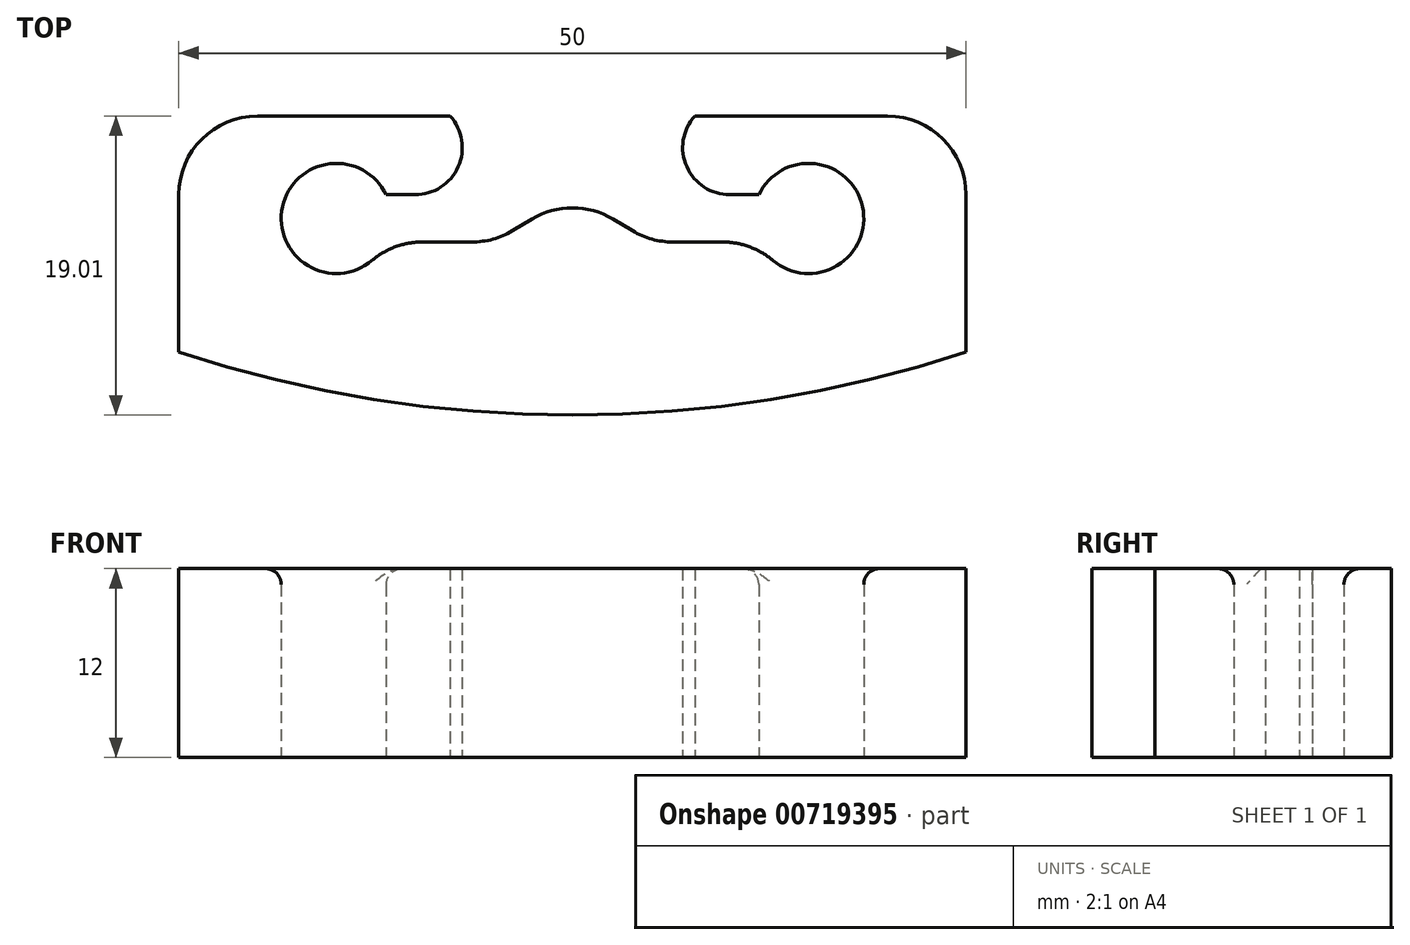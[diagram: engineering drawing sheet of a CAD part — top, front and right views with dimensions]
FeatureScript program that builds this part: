
annotation { "Feature Type Name" : "Feature", "Feature Type Description" : "" }
export const myFeature = defineFeature(function(context is Context, id is Id, definition is map)
    precondition{}
    {
        {
            var Q0;
            Q0=qCreatedBy(makeId("Top.planeOp"),FACE);
            var sketch = newSketch(context, id + "F0", { "sketchPlane" : qUnion([Q0])});
            skLineSegment(sketch, "E0", {"start": v(-25, -8.5) * mm, "end": v(-25, 1.5) * mm});
            skLineSegment(sketch, "E1", {"start": v(-20, 6.5) * mm, "end": v(-7.77, 6.5) * mm});
            skLineSegment(sketch, "E2", {"start": v(-10, 1.5) * mm, "end": v(-11.84, 1.5) * mm});
            skLineSegment(sketch, "E3", {"start": v(-9.52, -1.5) * mm, "end": v(-6.38, -1.5) * mm});
            skLineSegment(sketch, "E4", {"start": v(-3.81, -0.79) * mm, "end": v(-2.57, -0.04) * mm});
            skArc(sketch, "E5", {"start": v(-11.84, 1.5) * mm, "mid": v(-18.42, 0.74) * mm, "end": v(-12.74, -2.68) * mm});
            skArc(sketch, "E6", {"start": v(-10, 1.5) * mm, "mid": v(-7.26, 3.28) * mm, "end": v(-7.77, 6.5) * mm});
            skLineSegment(sketch, "E7.MirrorCS", {"start": v(9.52, -1.5) * mm, "end": v(6.38, -1.5) * mm});
            skLineSegment(sketch, "E8.MirrorCS", {"start": v(3.81, -0.79) * mm, "end": v(2.57, -0.04) * mm});
            skLineSegment(sketch, "E9.MirrorCS", {"start": v(20, 6.5) * mm, "end": v(7.77, 6.5) * mm});
            skLineSegment(sketch, "E10.MirrorCS", {"start": v(10, 1.5) * mm, "end": v(11.84, 1.5) * mm});
            skLineSegment(sketch, "E11.MirrorCS", {"start": v(25, -8.5) * mm, "end": v(25, 1.5) * mm});
            skArc(sketch, "E12.MirrorCS", {"start": v(11.84, 1.5) * mm, "mid": v(18.42, 0.74) * mm, "end": v(12.74, -2.68) * mm});
            skArc(sketch, "E13.MirrorCS", {"start": v(10, 1.5) * mm, "mid": v(7.26, 3.28) * mm, "end": v(7.77, 6.5) * mm});
            skArc(sketch, "E14", {"start": v(-25, -8.5) * mm, "mid": v(0, -12.5) * mm, "end": v(25, -8.5) * mm});
            skLineSegment(sketch, "E15", {"start": v(-30.94, 0) * mm, "end": v(26.36, 0) * mm, "construction": true});
            skPoint(sketch, "E16.visualSharp", {"position": v(-25, 6.5) * mm});
            skArc(sketch, "E16.filletArc", {"start": v(-20, 6.5) * mm, "mid": v(-23.54, 5.04) * mm, "end": v(-25, 1.5) * mm});
            skPoint(sketch, "E17.visualSharp", {"position": v(25, 6.5) * mm});
            skArc(sketch, "E17.filletArc", {"start": v(25, 1.5) * mm, "mid": v(23.54, 5.04) * mm, "end": v(20, 6.5) * mm});
            skPoint(sketch, "E18.visualSharp", {"position": v(-5, -1.5) * mm});
            skArc(sketch, "E18.filletArc", {"start": v(-6.38, -1.5) * mm, "mid": v(-5.05, -1.32) * mm, "end": v(-3.81, -0.79) * mm});
            skPoint(sketch, "E19.visualSharp", {"position": v(0, 1.5) * mm});
            skArc(sketch, "E19.filletArc", {"start": v(2.57, -0.04) * mm, "mid": v(0, 0.67) * mm, "end": v(-2.57, -0.04) * mm});
            skPoint(sketch, "E20.visualSharp", {"position": v(5, -1.5) * mm});
            skArc(sketch, "E20.filletArc", {"start": v(3.81, -0.79) * mm, "mid": v(5.05, -1.32) * mm, "end": v(6.38, -1.5) * mm});
            skPoint(sketch, "E21.visualSharp", {"position": v(11.84, -1.5) * mm});
            skArc(sketch, "E21.filletArc", {"start": v(12.74, -2.68) * mm, "mid": v(11.24, -1.8) * mm, "end": v(9.52, -1.5) * mm});
            skPoint(sketch, "E22.visualSharp", {"position": v(-11.84, -1.5) * mm});
            skArc(sketch, "E22.filletArc", {"start": v(-9.52, -1.5) * mm, "mid": v(-11.24, -1.8) * mm, "end": v(-12.74, -2.68) * mm});
            skSolve(sketch);
        }
        {
            var Q0;
            Q0 = qSketchRegion(id + "F0", true);
            extrude(context, id + "F1", {"entities" : qUnion([Q0]), "depth" : 12 * mm, "offsetDistance" : 25 * mm});
        }
        {
            var Q0;
            Q0=makeQuery(id+"F1.opExtrude","CAP_EDGE",EDGE,{"disambiguationData":[OSD([sQuery(id+"F0.wireOp",EDGE,"E5")])],"isStart":false});
            var Q1;
            Q1=makeQuery(id+"F1.opExtrude","CAP_EDGE",EDGE,{"disambiguationData":[OSD([sQuery(id+"F0.wireOp",EDGE,"E12.MirrorCS")])],"isStart":false});
            fillet(context, id + "F2", {"entities" : qUnion([Q0, Q1]), "radius" : 1 * mm, "allowEdgeOverflow" : false});
        }
    });
